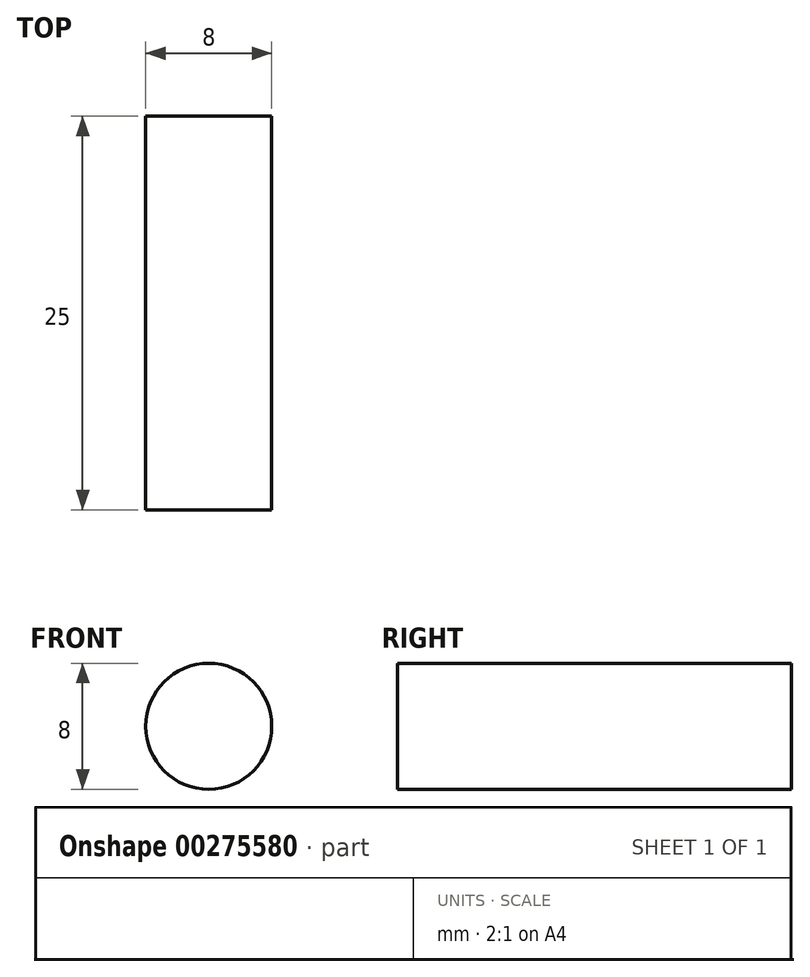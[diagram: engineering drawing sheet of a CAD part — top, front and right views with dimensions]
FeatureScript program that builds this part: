
annotation { "Feature Type Name" : "Feature", "Feature Type Description" : "" }
export const myFeature = defineFeature(function(context is Context, id is Id, definition is map)
    precondition{}
    {
        {
            var Q0;
            Q0=qCreatedBy(makeId("Front.planeOp"),FACE);
            var sketch = newSketch(context, id + "F0", { "sketchPlane" : qUnion([Q0])});
            skCircle(sketch, "E0", {"center": v(0, 0) * mm, "radius": 4 * mm});
            skSolve(sketch);
        }
        {
            var Q0;
            Q0 = qSketchRegion(id + "F0", true);
            extrude(context, id + "F1", {"entities" : qUnion([Q0]), "endBound" : BoundingType.SYMMETRIC, "depth" : 25 * mm});
        }
    });
